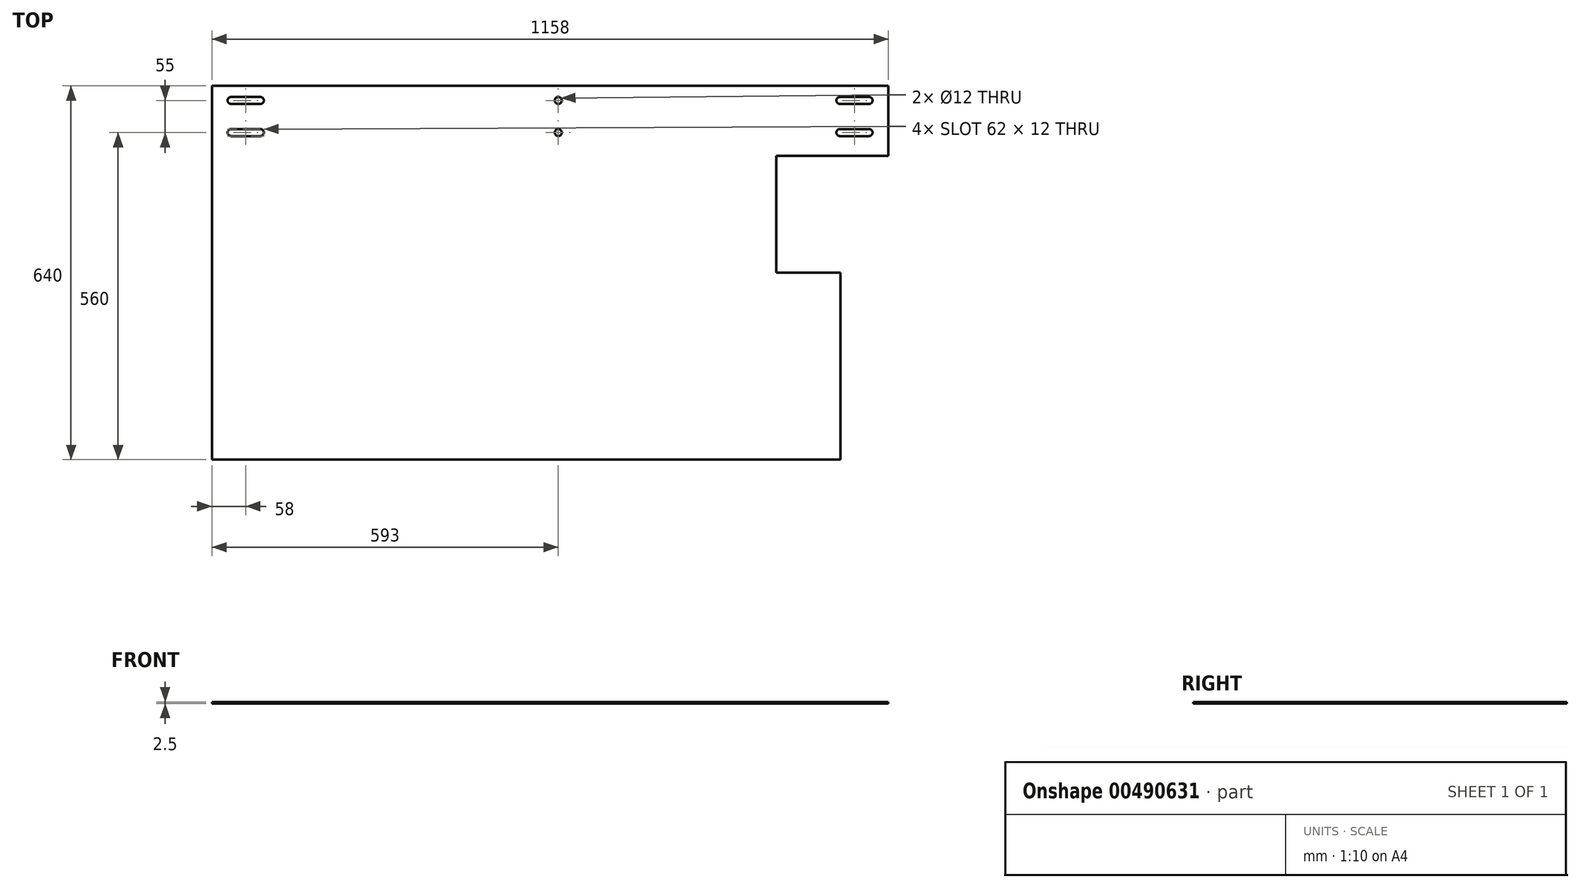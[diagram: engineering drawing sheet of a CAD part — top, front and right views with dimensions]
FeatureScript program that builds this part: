
annotation { "Feature Type Name" : "Feature", "Feature Type Description" : "" }
export const myFeature = defineFeature(function(context is Context, id is Id, definition is map)
    precondition{}
    {
        {
            var Q0;
            Q0=qCreatedBy(makeId("Top.planeOp"),FACE);
            var sketch = newSketch(context, id + "F0", { "sketchPlane" : qUnion([Q0])});
            skLineSegment(sketch, "E0", {"start": v(0, 0) * mm, "end": v(1076, 0) * mm});
            skLineSegment(sketch, "E1", {"start": v(1076, 0) * mm, "end": v(1076, 320) * mm});
            skLineSegment(sketch, "E2", {"start": v(1076, 320) * mm, "end": v(966, 320) * mm});
            skLineSegment(sketch, "E3", {"start": v(1158, 520) * mm, "end": v(1158, 640) * mm});
            skLineSegment(sketch, "E4", {"start": v(1158, 640) * mm, "end": v(0, 640) * mm});
            skLineSegment(sketch, "E5", {"start": v(0, 640) * mm, "end": v(0, 0) * mm});
            skLineSegment(sketch, "E6", {"start": v(33, 621) * mm, "end": v(83, 621) * mm});
            skLineSegment(sketch, "E7", {"start": v(33, 609) * mm, "end": v(83, 609) * mm});
            skArc(sketch, "E8", {"start": v(33, 621) * mm, "mid": v(27, 615) * mm, "end": v(33, 609) * mm});
            skArc(sketch, "E9", {"start": v(83, 621) * mm, "mid": v(89, 615) * mm, "end": v(83, 609) * mm});
            skLineSegment(sketch, "E10", {"start": v(58, 621) * mm, "end": v(58, 609) * mm, "construction": true});
            skLineSegment(sketch, "E11.0.1.0", {"start": v(33, 566) * mm, "end": v(83, 566) * mm});
            skArc(sketch, "E11.0.1.1", {"start": v(33, 566) * mm, "mid": v(27, 560) * mm, "end": v(33, 554) * mm});
            skLineSegment(sketch, "E11.0.1.2", {"start": v(33, 554) * mm, "end": v(83, 554) * mm});
            skArc(sketch, "E11.0.1.3", {"start": v(83, 566) * mm, "mid": v(89, 560) * mm, "end": v(83, 554) * mm});
            skLineSegment(sketch, "E11.1.0.0", {"start": v(1075, 621) * mm, "end": v(1125, 621) * mm});
            skArc(sketch, "E11.1.0.1", {"start": v(1075, 621) * mm, "mid": v(1069, 615) * mm, "end": v(1075, 609) * mm});
            skLineSegment(sketch, "E11.1.0.2", {"start": v(1075, 609) * mm, "end": v(1125, 609) * mm});
            skArc(sketch, "E11.1.0.3", {"start": v(1125, 621) * mm, "mid": v(1131, 615) * mm, "end": v(1125, 609) * mm});
            skLineSegment(sketch, "E11.1.1.0", {"start": v(1075, 566) * mm, "end": v(1125, 566) * mm});
            skArc(sketch, "E11.1.1.1", {"start": v(1075, 566) * mm, "mid": v(1069, 560) * mm, "end": v(1075, 554) * mm});
            skLineSegment(sketch, "E11.1.1.2", {"start": v(1075, 554) * mm, "end": v(1125, 554) * mm});
            skArc(sketch, "E11.1.1.3", {"start": v(1125, 566) * mm, "mid": v(1131, 560) * mm, "end": v(1125, 554) * mm});
            skLineSegment(sketch, "E11.direction1", {"start": v(33, 609) * mm, "end": v(1075, 609) * mm, "construction": true});
            skLineSegment(sketch, "E11.direction2", {"start": v(33, 609) * mm, "end": v(33, 554) * mm, "construction": true});
            skLineSegment(sketch, "E12", {"start": v(1100, 621) * mm, "end": v(1100, 609) * mm, "construction": true});
            skCircle(sketch, "E13", {"center": v(593, 615) * mm, "radius": 6 * mm});
            skCircle(sketch, "E14", {"center": v(593, 560) * mm, "radius": 6 * mm});
            skLineSegment(sketch, "E15.trimOffspring", {"start": v(966, 520) * mm, "end": v(1158, 520) * mm});
            skLineSegment(sketch, "E16.trimOffspring", {"start": v(966, 320) * mm, "end": v(966, 520) * mm});
            skSolve(sketch);
        }
        {
            var Q0;
            Q0=makeQuery(id+"F0.imprint","IMPRINT",FACE,{"disambiguationData":[TD([[makeQuery(id+"F0.imprint","IMPRINT",EDGE,{"derivedFrom":sQuery(id+"F0.wireOp",EDGE,"E0")}),1.0]])]});
            extrude(context, id + "F1", {"entities" : qUnion([Q0]), "depth" : 2.5 * mm});
        }
    });
